# Revit family: RRHS Tapered
name_source: partatom
category: Generic Models
revit_build: Autodesk Revit 2018 (Build: 20190510_1515(x64)
units: mm (PartAtom-declared; Revit-internal decimal feet)

## family parameters
Always vertical = No
Can host rebar = No
Cut with Voids When Loaded = No
Part Type = Normal
Room Calculation Point = No
Round Connector Dimension = Use Diameter
Shared = Yes
Work Plane-Based = Yes

## types (5) — shared parameters
Default Elevation = 48 "
Flat Gasket = GSK002001 : GSK002001-01
Rack Slot Gasket = RRRG38
Spacer Material = <By Category>

## per-type parameters (varying)
| type | Description | Inside Diameter | Inside Radius | Length |
| RRHS381T | Spacer Tapered Hygienic 304 3/8-16 Threaded Hole 1 Inch long | 0.375 " | 0.188 " | 1 " |
| RRHS382T | Spacer Tapered Hygienic 304 3/8-16 Threaded Hole 2 Inch long | 0.375 " | 0.188 " | 2 " |
| RRHS141T | Spacer Tapered Hygienic 304 1/4-20 Threaded Hole 1 Inch long | 0.25 " | 0.125 " | 1 " |
| RRHS142T | Spacer Tapered Hygienic 304 1/4-20 Threaded Hole 2 Inch long | 0.25 " | 0.125 " | 2 " |
| RRHS122T | Spacer Tapered Hygienic 304 1/2-13 Threaded Hole 2 Inch long | 0.5 " | 0.25 " | 2 " |

note: column(s) folded — value = type name in every type: Catalog Number

## geometry (parser evidence)
native form markers: Sweep x7
no freeform markers — native parametric forms only
